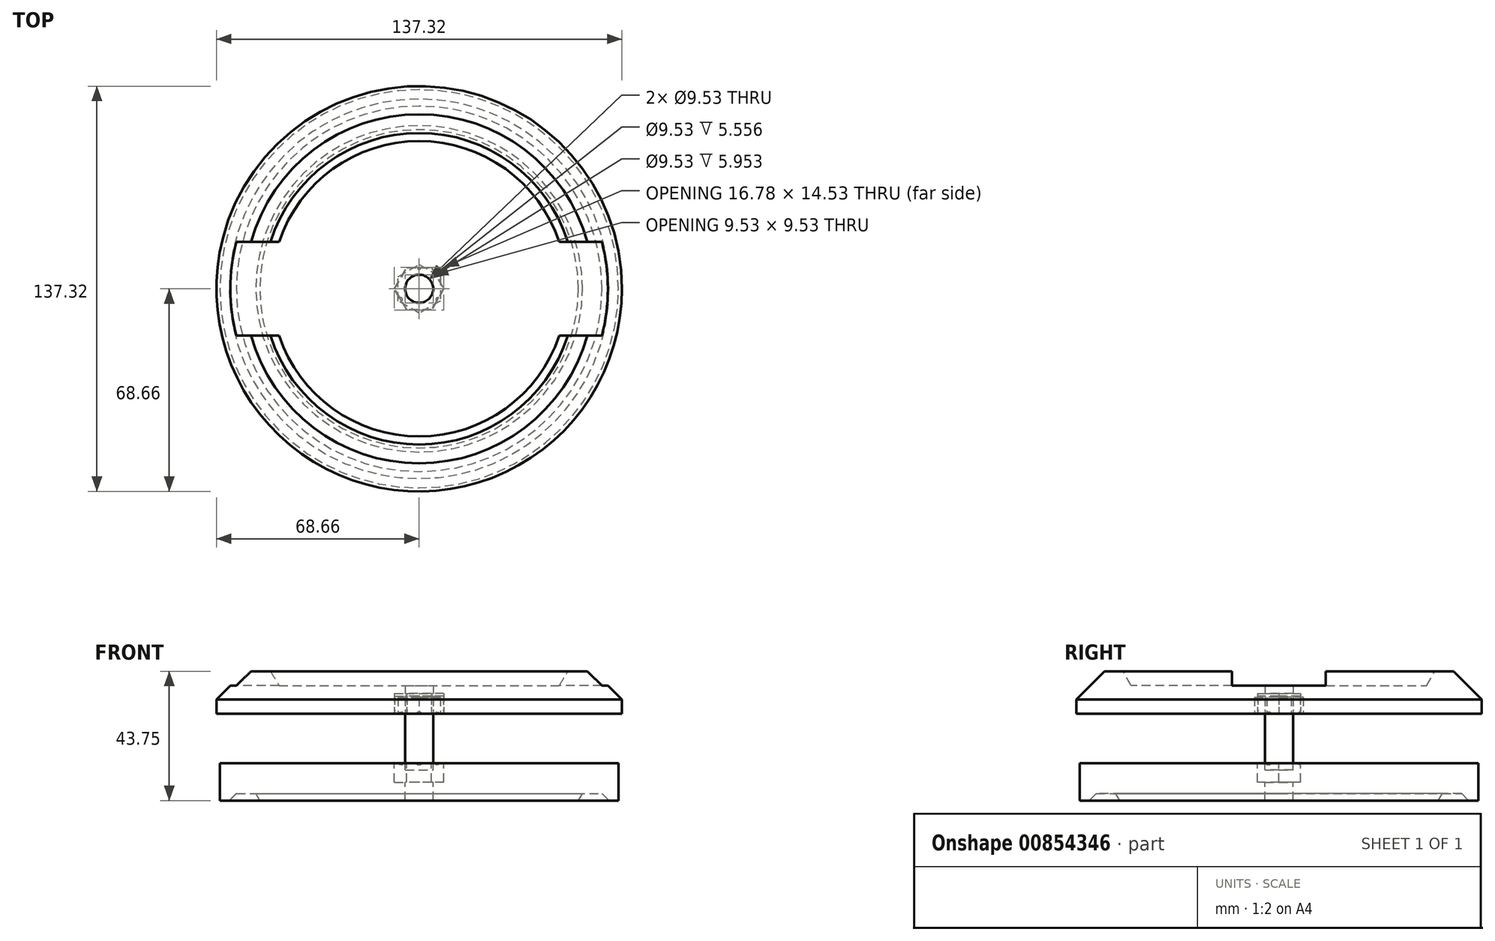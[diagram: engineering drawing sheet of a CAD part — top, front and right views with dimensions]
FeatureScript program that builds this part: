
annotation { "Feature Type Name" : "Feature", "Feature Type Description" : "" }
export const myFeature = defineFeature(function(context is Context, id is Id, definition is map)
    precondition{}
    {
        {
            var Q0;
            Q0=qCreatedBy(makeId("Front.planeOp"),FACE);
            var sketch = newSketch(context, id + "F0", { "sketchPlane" : qUnion([Q0])});
            skLineSegment(sketch, "E0", {"start": v(-68.66, 4.76) * mm, "end": v(-59.14, 14.29) * mm});
            skLineSegment(sketch, "E1", {"start": v(-59.14, 14.29) * mm, "end": v(-52.79, 14.29) * mm});
            skLineSegment(sketch, "E2", {"start": v(-52.79, 14.29) * mm, "end": v(-50.04, 9.53) * mm});
            skLineSegment(sketch, "E3", {"start": v(-50.04, 9.53) * mm, "end": v(0, 9.53) * mm});
            skLineSegment(sketch, "E4", {"start": v(0, 9.53) * mm, "end": v(0, 0) * mm});
            skLineSegment(sketch, "E5", {"start": v(0, 0) * mm, "end": v(-68.66, 0) * mm});
            skLineSegment(sketch, "E6", {"start": v(-68.66, 4.76) * mm, "end": v(-68.66, 0) * mm});
            skSolve(sketch);
        }
        {
            var Q0;
            Q0 = qSketchRegion(id + "F0", true);
            var Q1;
            Q1=sQuery(id+"F0.wireOp",EDGE,"E4");
            revolve(context, id + "F1", {"surfaceOperationType" : NewSurfaceOperationType.NEW, "entities" : qUnion([Q0]), "axis" : qUnion([Q1]), "revolveType" : RevolveType.FULL});
        }
        {
            var Q0;
            Q0=qCreatedBy(makeId("Front.planeOp"),FACE);
            var sketch = newSketch(context, id + "F2", { "sketchPlane" : qUnion([Q0])});
            skLineSegment(sketch, "E7", {"start": v(0, -16.76) * mm, "end": v(-67.47, -16.76) * mm});
            skLineSegment(sketch, "E8", {"start": v(-67.47, -16.76) * mm, "end": v(-67.47, -29.46) * mm});
            skLineSegment(sketch, "E9", {"start": v(-67.47, -29.46) * mm, "end": v(-64.3, -29.46) * mm});
            skLineSegment(sketch, "E10", {"start": v(-64.3, -29.46) * mm, "end": v(-61.91, -27.08) * mm});
            skLineSegment(sketch, "E11", {"start": v(-61.91, -27.08) * mm, "end": v(-55.3, -27.08) * mm});
            skLineSegment(sketch, "E12", {"start": v(-55.3, -27.08) * mm, "end": v(-53.93, -29.46) * mm});
            skLineSegment(sketch, "E13", {"start": v(-53.93, -29.46) * mm, "end": v(0, -29.46) * mm});
            skLineSegment(sketch, "E14", {"start": v(0, -29.46) * mm, "end": v(0, -16.76) * mm});
            skSolve(sketch);
        }
        {
            var Q0;
            Q0 = qSketchRegion(id + "F2", true);
            var Q1;
            Q1=sQuery(id+"F2.wireOp",EDGE,"E14");
            revolve(context, id + "F3", {"surfaceOperationType" : NewSurfaceOperationType.NEW, "entities" : qUnion([Q0]), "axis" : qUnion([Q1]), "revolveType" : RevolveType.FULL});
        }
        {
            var Q0;
            Q0=makeQuery(id+"F1.opRevolve","SWEPT_FACE",FACE,{"disambiguationData":[OSD([sQuery(id+"F0.wireOp",EDGE,"E5")])]});
            var sketch = newSketch(context, id + "F4", { "sketchPlane" : qUnion([Q0])});
            skCircle(sketch, "E15.cCircle", {"center": v(0, 0) * mm, "radius": 7.26 * mm, "construction": true});
            skLineSegment(sketch, "E15.0", {"start": v(4.2, -7.26) * mm, "end": v(-4.2, -7.26) * mm});
            skLineSegment(sketch, "E15.1", {"start": v(-4.2, -7.26) * mm, "end": v(-8.39, 0) * mm});
            skLineSegment(sketch, "E15.2", {"start": v(-8.39, 0) * mm, "end": v(-4.2, 7.26) * mm});
            skLineSegment(sketch, "E15.3", {"start": v(-4.2, 7.26) * mm, "end": v(4.2, 7.26) * mm});
            skLineSegment(sketch, "E15.4", {"start": v(4.2, 7.26) * mm, "end": v(8.39, 0) * mm});
            skLineSegment(sketch, "E15.5", {"start": v(8.39, 0) * mm, "end": v(4.2, -7.26) * mm});
            skPoint(sketch, "E15.0.midPoint", {"position": v(0, -7.26) * mm});
            skSolve(sketch);
        }
        {
            var Q0;
            Q0 = qSketchRegion(id + "F4", true);
            extrude(context, id + "F5", {"entities" : qUnion([Q0]), "operationType" : NewBodyOperationType.REMOVE, "oppositeDirection" : true, "depth" : 6.86 * mm, "offsetDistance" : 25.4 * mm});
        }
        {
            var Q0;
            Q0=makeQuery(id+"F3.opRevolve","SWEPT_FACE",FACE,{"disambiguationData":[OSD([sQuery(id+"F2.wireOp",EDGE,"E7")])]});
            var sketch = newSketch(context, id + "F6", { "sketchPlane" : qUnion([Q0])});
            skCircle(sketch, "E16.cCircle", {"center": v(0, 0) * mm, "radius": 7.26 * mm, "construction": true});
            skLineSegment(sketch, "E16.0", {"start": v(4.2, -7.26) * mm, "end": v(-4.2, -7.26) * mm});
            skLineSegment(sketch, "E16.1", {"start": v(-4.2, -7.26) * mm, "end": v(-8.39, 0) * mm});
            skLineSegment(sketch, "E16.2", {"start": v(-8.39, 0) * mm, "end": v(-4.2, 7.26) * mm});
            skLineSegment(sketch, "E16.3", {"start": v(-4.2, 7.26) * mm, "end": v(4.2, 7.26) * mm});
            skLineSegment(sketch, "E16.4", {"start": v(4.2, 7.26) * mm, "end": v(8.39, 0) * mm});
            skLineSegment(sketch, "E16.5", {"start": v(8.39, 0) * mm, "end": v(4.2, -7.26) * mm});
            skPoint(sketch, "E16.0.midPoint", {"position": v(0, -7.26) * mm});
            skSolve(sketch);
        }
        {
            var Q0;
            Q0 = qSketchRegion(id + "F6", true);
            extrude(context, id + "F7", {"entities" : qUnion([Q0]), "operationType" : NewBodyOperationType.REMOVE, "oppositeDirection" : true, "depth" : 6.48 * mm, "offsetDistance" : 25.4 * mm});
        }
        {
            var Q0;
            Q0=makeQuery(id+"F3.opRevolve","SWEPT_FACE",FACE,{"disambiguationData":[OSD([sQuery(id+"F2.wireOp",EDGE,"E7")])]});
            var sketch = newSketch(context, id + "F8", { "sketchPlane" : qUnion([Q0])});
            skCircle(sketch, "E17", {"center": v(0, 0) * mm, "radius": 4.76 * mm});
            skSolve(sketch);
        }
        {
            var Q0;
            Q0 = qSketchRegion(id + "F8", true);
            extrude(context, id + "F9", {"entities" : qUnion([Q0]), "operationType" : NewBodyOperationType.REMOVE, "endBound" : BoundingType.THROUGH_ALL, "oppositeDirection" : true, "depth" : 25.4 * mm, "offsetDistance" : 25.4 * mm});
        }
        {
            var Q0;
            Q0=makeQuery(id+"F1.opRevolve","SWEPT_FACE",FACE,{"disambiguationData":[OSD([sQuery(id+"F0.wireOp",EDGE,"E1")])]});
            var sketch = newSketch(context, id + "F10", { "sketchPlane" : qUnion([Q0])});
            skLineSegment(sketch, "E18.bottom", {"start": v(82.55, -15.87) * mm, "end": v(-82.55, -15.88) * mm});
            skLineSegment(sketch, "E18.top", {"start": v(82.55, 15.88) * mm, "end": v(-82.55, 15.88) * mm});
            skLineSegment(sketch, "E18.left", {"start": v(82.55, -15.87) * mm, "end": v(82.55, 15.88) * mm});
            skLineSegment(sketch, "E18.right", {"start": v(-82.55, -15.88) * mm, "end": v(-82.55, 15.87) * mm});
            skPoint(sketch, "E18.middle", {"position": v(0, 0) * mm});
            skSolve(sketch);
        }
        {
            var Q0;
            Q0 = qSketchRegion(id + "F10", true);
            extrude(context, id + "F11", {"entities" : qUnion([Q0]), "operationType" : NewBodyOperationType.REMOVE, "oppositeDirection" : true, "depth" : 4.76 * mm, "offsetDistance" : 25.4 * mm});
        }
        {
            var Q0;
            Q0=makeQuery(id+"F1.opRevolve","SWEPT_FACE",FACE,{"disambiguationData":[OSD([sQuery(id+"F0.wireOp",EDGE,"E5")])]});
            var sketch = newSketch(context, id + "F12", { "sketchPlane" : qUnion([Q0])});
            skArc(sketch, "E19", {"start": v(-6.6, 3.08) * mm, "mid": v(-5.74, 3.31) * mm, "end": v(-5.97, 4.18) * mm});
            skLineSegment(sketch, "E20", {"start": v(-5.97, 4.18) * mm, "end": v(-6.6, 3.08) * mm});
            skArc(sketch, "E21.1.0", {"start": v(0.64, -7.26) * mm, "mid": v(0, -6.63) * mm, "end": v(-0.64, -7.26) * mm});
            skLineSegment(sketch, "E21.1.1", {"start": v(-0.64, -7.26) * mm, "end": v(0.63, -7.26) * mm});
            skArc(sketch, "E21.2.0", {"start": v(5.97, 4.18) * mm, "mid": v(5.74, 3.31) * mm, "end": v(6.6, 3.08) * mm});
            skLineSegment(sketch, "E21.2.1", {"start": v(6.6, 3.08) * mm, "end": v(5.97, 4.18) * mm});
            skPoint(sketch, "E21.center", {"position": v(0, 0) * mm});
            skSolve(sketch);
        }
        {
            var Q0;
            Q0 = qSketchRegion(id + "F12", true);
            extrude(context, id + "F13", {"entities" : qUnion([Q0]), "operationType" : NewBodyOperationType.ADD, "oppositeDirection" : true, "depth" : 0.5 * mm, "offsetDistance" : 25.4 * mm});
        }
        {
            var Q0;
            Q0=makeQuery(id+"F3.opRevolve","SWEPT_FACE",FACE,{"disambiguationData":[OSD([sQuery(id+"F2.wireOp",EDGE,"E7")])]});
            var sketch = newSketch(context, id + "F14", { "sketchPlane" : qUnion([Q0])});
            skArc(sketch, "E22", {"start": v(-5.97, -4.18) * mm, "mid": v(-5.74, -3.31) * mm, "end": v(-6.6, -3.08) * mm});
            skLineSegment(sketch, "E23", {"start": v(-6.6, -3.08) * mm, "end": v(-5.97, -4.18) * mm});
            skArc(sketch, "E24.1.0", {"start": v(6.6, -3.08) * mm, "mid": v(5.74, -3.31) * mm, "end": v(5.97, -4.18) * mm});
            skLineSegment(sketch, "E24.1.1", {"start": v(5.97, -4.18) * mm, "end": v(6.6, -3.08) * mm});
            skArc(sketch, "E24.2.0", {"start": v(-0.63, 7.26) * mm, "mid": v(0, 6.63) * mm, "end": v(0.64, 7.26) * mm});
            skLineSegment(sketch, "E24.2.1", {"start": v(0.64, 7.26) * mm, "end": v(-0.63, 7.26) * mm});
            skPoint(sketch, "E24.center", {"position": v(0, 0) * mm});
            skSolve(sketch);
        }
        {
            var Q0;
            Q0 = qSketchRegion(id + "F14", true);
            extrude(context, id + "F15", {"entities" : qUnion([Q0]), "operationType" : NewBodyOperationType.ADD, "oppositeDirection" : true, "depth" : 0.5 * mm, "offsetDistance" : 25.4 * mm});
        }
        {
            var Q0;
            Q0=qCreatedBy(makeId("Top.planeOp"),FACE);
            var sketch = newSketch(context, id + "F16", { "sketchPlane" : qUnion([Q0])});
            skCircle(sketch, "E25.cCircle", {"center": v(0, 0) * mm, "radius": 7.14 * mm, "construction": true});
            skLineSegment(sketch, "E25.0", {"start": v(4.12, -7.14) * mm, "end": v(-4.12, -7.14) * mm});
            skLineSegment(sketch, "E25.1", {"start": v(-4.12, -7.14) * mm, "end": v(-8.25, 0) * mm});
            skLineSegment(sketch, "E25.2", {"start": v(-8.25, 0) * mm, "end": v(-4.12, 7.14) * mm});
            skLineSegment(sketch, "E25.3", {"start": v(-4.12, 7.14) * mm, "end": v(4.12, 7.14) * mm});
            skLineSegment(sketch, "E25.4", {"start": v(4.12, 7.14) * mm, "end": v(8.25, 0) * mm});
            skLineSegment(sketch, "E25.5", {"start": v(8.25, 0) * mm, "end": v(4.12, -7.14) * mm});
            skPoint(sketch, "E25.0.midPoint", {"position": v(0, -7.14) * mm});
            skSolve(sketch);
        }
        {
            var Q0;
            Q0 = qSketchRegion(id + "F16", true);
            extrude(context, id + "F17", {"entities" : qUnion([Q0]), "depth" : 5.95 * mm, "offsetDistance" : 25.4 * mm});
        }
        {
            var Q0;
            Q0=makeQuery(id+"F17.opExtrude","CAP_FACE",FACE,{"disambiguationData":[OSD([sQuery(id+"F16.wireOp",EDGE,"E25.0"),sQuery(id+"F16.wireOp",EDGE,"E25.1"),sQuery(id+"F16.wireOp",EDGE,"E25.2"),sQuery(id+"F16.wireOp",EDGE,"E25.3"),sQuery(id+"F16.wireOp",EDGE,"E25.4"),sQuery(id+"F16.wireOp",EDGE,"E25.5")])],"isStart":true});
            var sketch = newSketch(context, id + "F18", { "sketchPlane" : qUnion([Q0])});
            skCircle(sketch, "E26", {"center": v(0, 0) * mm, "radius": 4.76 * mm});
            skSolve(sketch);
        }
        {
            var Q0;
            Q0 = qSketchRegion(id + "F18", true);
            extrude(context, id + "F19", {"entities" : qUnion([Q0]), "operationType" : NewBodyOperationType.ADD, "depth" : 19.05 * mm, "offsetDistance" : 25.4 * mm});
        }
        {
            var Q0;
            Q0=qCreatedBy(makeId("Top.planeOp"),FACE);
            var sketch = newSketch(context, id + "F20", { "sketchPlane" : qUnion([Q0])});
            skCircle(sketch, "E27.cCircle", {"center": v(0, 0) * mm, "radius": 7.14 * mm, "construction": true});
            skLineSegment(sketch, "E27.0", {"start": v(7.14, 4.12) * mm, "end": v(7.14, -4.12) * mm});
            skLineSegment(sketch, "E27.1", {"start": v(7.14, -4.12) * mm, "end": v(0, -8.25) * mm});
            skLineSegment(sketch, "E27.2", {"start": v(0, -8.25) * mm, "end": v(-7.14, -4.12) * mm});
            skLineSegment(sketch, "E27.3", {"start": v(-7.14, -4.12) * mm, "end": v(-7.14, 4.12) * mm});
            skLineSegment(sketch, "E27.4", {"start": v(-7.14, 4.12) * mm, "end": v(0, 8.25) * mm});
            skLineSegment(sketch, "E27.5", {"start": v(0, 8.25) * mm, "end": v(7.14, 4.12) * mm});
            skPoint(sketch, "E27.0.midPoint", {"position": v(7.14, 0) * mm});
            skSolve(sketch);
        }
        {
            var Q0;
            Q0 = qSketchRegion(id + "F20", true);
            extrude(context, id + "F21", {"entities" : qUnion([Q0]), "depth" : 5.56 * mm, "offsetDistance" : 25.4 * mm});
        }
        {
            var Q0;
            Q0=makeQuery(id+"F21.opExtrude","CAP_FACE",FACE,{"disambiguationData":[OSD([sQuery(id+"F20.wireOp",EDGE,"E27.0"),sQuery(id+"F20.wireOp",EDGE,"E27.1"),sQuery(id+"F20.wireOp",EDGE,"E27.2"),sQuery(id+"F20.wireOp",EDGE,"E27.3"),sQuery(id+"F20.wireOp",EDGE,"E27.4"),sQuery(id+"F20.wireOp",EDGE,"E27.5")])],"isStart":true});
            var sketch = newSketch(context, id + "F22", { "sketchPlane" : qUnion([Q0])});
            skCircle(sketch, "E28", {"center": v(0, 0) * mm, "radius": 4.76 * mm});
            skSolve(sketch);
        }
        {
            var Q0;
            Q0 = qSketchRegion(id + "F22", true);
            extrude(context, id + "F23", {"entities" : qUnion([Q0]), "operationType" : NewBodyOperationType.REMOVE, "endBound" : BoundingType.THROUGH_ALL, "oppositeDirection" : true, "depth" : 25.4 * mm, "offsetDistance" : 25.4 * mm});
        }
    });
